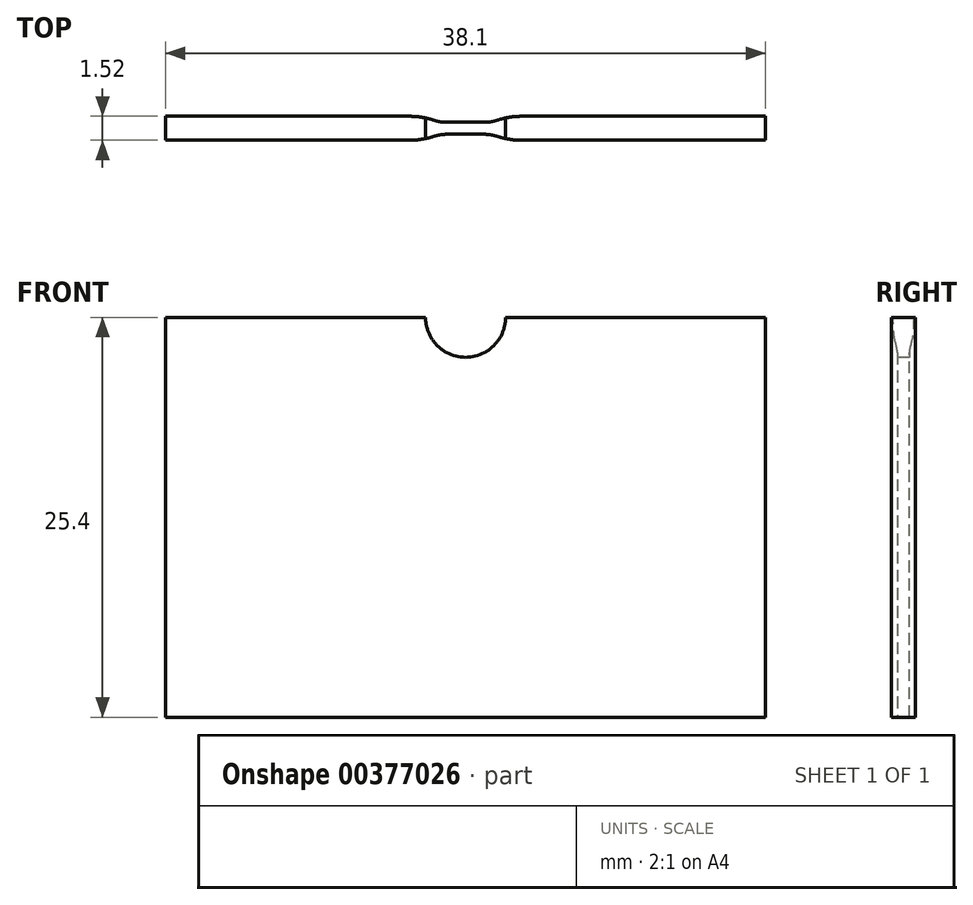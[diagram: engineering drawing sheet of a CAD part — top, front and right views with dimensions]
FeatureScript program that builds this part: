
annotation { "Feature Type Name" : "Feature", "Feature Type Description" : "" }
export const myFeature = defineFeature(function(context is Context, id is Id, definition is map)
    precondition{}
    {
        {
            var Q0;
            Q0=qCreatedBy(makeId("Front.planeOp"),FACE);
            var sketch = newSketch(context, id + "F0", { "sketchPlane" : qUnion([Q0])});
            skLineSegment(sketch, "E0.bottom", {"start": v(0, 0) * mm, "end": v(38.1, 0) * mm});
            skLineSegment(sketch, "E0.top", {"start": v(0, 25.4) * mm, "end": v(38.1, 25.4) * mm});
            skLineSegment(sketch, "E0.left", {"start": v(0, 0) * mm, "end": v(0, 25.4) * mm});
            skLineSegment(sketch, "E0.right", {"start": v(38.1, 0) * mm, "end": v(38.1, 25.4) * mm});
            skSolve(sketch);
        }
        {
            var Q0;
            Q0=makeQuery(id+"F0.imprint","IMPRINT",FACE,{"disambiguationData":[TD([[makeQuery(id+"F0.imprint","IMPRINT",EDGE,{"derivedFrom":sQuery(id+"F0.wireOp",EDGE,"E0.bottom")}),1.0]])]});
            extrude(context, id + "F1", {"entities" : qUnion([Q0]), "depth" : 1.52 * mm});
        }
        {
            var Q0;
            Q0=makeQuery(id+"F1.opExtrude","CAP_FACE",FACE,{"disambiguationData":[OSD([sQuery(id+"F0.wireOp",EDGE,"E0.bottom"),sQuery(id+"F0.wireOp",EDGE,"E0.top"),sQuery(id+"F0.wireOp",EDGE,"E0.left"),sQuery(id+"F0.wireOp",EDGE,"E0.right")])],"isStart":false});
            var sketch = newSketch(context, id + "F2", { "sketchPlane" : qUnion([Q0])});
            skArc(sketch, "E1", {"start": v(16.5, 25.4) * mm, "mid": v(19.05, 22.86) * mm, "end": v(21.59, 25.4) * mm});
            skLineSegment(sketch, "E2", {"start": v(16.5, 25.4) * mm, "end": v(21.59, 25.4) * mm});
            skSolve(sketch);
        }
        {
            var Q0;
            Q0 = qSketchRegion(id + "F2", true);
            extrude(context, id + "F3", {"entities" : qUnion([Q0]), "operationType" : NewBodyOperationType.REMOVE, "oppositeDirection" : true, "depth" : 25.4 * mm});
        }
        {
            var Q0;
            Q0=makeQuery(id+"F1.opExtrude","CAP_EDGE",EDGE,{"disambiguationData":[OSD([sQuery(id+"F0.wireOp",EDGE,"E0.right")])],"isStart":false});
            cPoint(context, id + "F4", {"entities" : qUnion([Q0]), "parameter" : 0.5});
        }
        {
            var Q0;
            Q0=makeQuery(id+"F1.opExtrude","CAP_EDGE",EDGE,{"disambiguationData":[OSD([sQuery(id+"F0.wireOp",EDGE,"E0.left")])],"isStart":false});
            cPoint(context, id + "F5", {"entities" : qUnion([Q0]), "parameter" : 0.5});
        }
        {
            var Q0;
            Q0=makeQuery(id+"F1.opExtrude","CAP_EDGE",EDGE,{"disambiguationData":[OSD([sQuery(id+"F0.wireOp",EDGE,"E0.right")])],"isStart":true});
            cPoint(context, id + "F6", {"entities" : qUnion([Q0]), "parameter" : 0.5});
        }
        {
            var Q0;
            Q0 = qCreatedBy(id + "F4" ,VERTEX);
            var Q1;
            Q1 = qCreatedBy(id + "F5" ,VERTEX);
            var Q2;
            Q2 = qCreatedBy(id + "F6" ,VERTEX);
            cPlane(context, id + "F7", {"entities" : qUnion([Q0, Q1, Q2]), "cplaneType" : CPlaneType.THREE_POINT, "offset" : 25.4 * mm, "width" : 152.4 * mm, "height" : 152.4 * mm});
        }
        {
            var Q0;
            Q0=qCreatedBy(makeId("Top.planeOp"),FACE);
            var sketch = newSketch(context, id + "F8", { "sketchPlane" : qUnion([Q0])});
            skLineSegment(sketch, "E3.0", {"start": v(0, -1.52) * mm, "end": v(16.51, -1.52) * mm});
            skLineSegment(sketch, "E4.0", {"start": v(0, 0) * mm, "end": v(16.51, 0) * mm});
            skLineSegment(sketch, "E5", {"start": v(16.51, -1.52) * mm, "end": v(16.51, -1.14) * mm});
            skLineSegment(sketch, "E6", {"start": v(16.51, -1.14) * mm, "end": v(21.59, -1.14) * mm});
            skLineSegment(sketch, "E7", {"start": v(21.59, -1.14) * mm, "end": v(21.59, -1.52) * mm});
            skLineSegment(sketch, "E8", {"start": v(21.59, 0) * mm, "end": v(21.59, -0.38) * mm});
            skLineSegment(sketch, "E9", {"start": v(21.59, -0.38) * mm, "end": v(16.51, -0.38) * mm});
            skLineSegment(sketch, "E10", {"start": v(16.51, -0.38) * mm, "end": v(16.51, 0) * mm});
            skLineSegment(sketch, "E11", {"start": v(16.51, -1.52) * mm, "end": v(21.59, -1.52) * mm});
            skLineSegment(sketch, "E12", {"start": v(21.59, 0) * mm, "end": v(16.51, 0) * mm});
            skSolve(sketch);
        }
        {
            var Q0;
            Q0 = qSketchRegion(id + "F8", true);
            extrude(context, id + "F9", {"entities" : qUnion([Q0]), "operationType" : NewBodyOperationType.REMOVE, "depth" : 25.4 * mm});
        }
        {
            var Q0;
            Q0=makeQuery(id+"F9.boolean.opBoolean","COPY",EDGE,{"derivedFrom":makeQuery(id+"F9.opExtrude","SWEPT_EDGE",EDGE,{"disambiguationData":[OSD([sQuery(id+"F8.wireOp",EDGE,"E5"),sQuery(id+"F8.wireOp",EDGE,"E6")])]})});
            var Q1;
            Q1=makeQuery(id+"F9.boolean.opBoolean","COPY",EDGE,{"derivedFrom":makeQuery(id+"F9.opExtrude","SWEPT_EDGE",EDGE,{"disambiguationData":[OSD([sQuery(id+"F8.wireOp",EDGE,"E6"),sQuery(id+"F8.wireOp",EDGE,"E7")])]})});
            var Q2;
            Q2=makeQuery(id+"F9.boolean.opBoolean","COPY",EDGE,{"derivedFrom":makeQuery(id+"F9.opExtrude","SWEPT_EDGE",EDGE,{"disambiguationData":[OSD([sQuery(id+"F8.wireOp",EDGE,"E8"),sQuery(id+"F8.wireOp",EDGE,"E9")])]})});
            var Q3;
            Q3=makeQuery(id+"F9.boolean.opBoolean","COPY",EDGE,{"derivedFrom":makeQuery(id+"F9.opExtrude","SWEPT_EDGE",EDGE,{"disambiguationData":[OSD([sQuery(id+"F8.wireOp",EDGE,"E9"),sQuery(id+"F8.wireOp",EDGE,"E10")])]})});
            fillet(context, id + "F10", {"entities" : qUnion([Q0, Q1, Q2, Q3]), "radius" : 2.54 * mm, "tangentPropagation" : true, "allowEdgeOverflow" : false});
        }
        {
            var Q0;
            {var subQ0=sQuery(id+"F0.wireOp",EDGE,"E0.bottom");var subQ1=sQuery(id+"F0.wireOp",EDGE,"E0.top");var subQ2=sQuery(id+"F0.wireOp",EDGE,"E0.left");var subQ3=sQuery(id+"F8.wireOp",EDGE,"E5");Q0=makeQuery(id+"F10.opFillet","BLEND_EDGE",EDGE,{"blendedFrom":[makeQuery(id+"F9.boolean.opBoolean","COPY",EDGE,{"derivedFrom":makeQuery(id+"F9.opExtrude","SWEPT_EDGE",EDGE,{"disambiguationData":[OSD([subQ3,sQuery(id+"F8.wireOp",EDGE,"E6")])]})}),makeQuery(id+"F9.boolean.opBoolean","SPLIT",FACE,{"disambiguationData":[TD([makeQuery(id+"F1.opExtrude","SWEPT_FACE",FACE,{"disambiguationData":[OSD([subQ2])]})])],"derivedFrom":makeQuery(id+"F1.opExtrude","CAP_FACE",FACE,{"disambiguationData":[OSD([subQ0,subQ1,subQ2,sQuery(id+"F0.wireOp",EDGE,"E0.right")])],"isStart":false})})],"blendedInto":[makeQuery(id+"F9.boolean.opBoolean","SPLIT",FACE,{"disambiguationData":[TD([makeQuery(id+"F1.opExtrude","SWEPT_FACE",FACE,{"disambiguationData":[OSD([subQ2])]})])],"derivedFrom":makeQuery(id+"F1.opExtrude","CAP_FACE",FACE,{"disambiguationData":[OSD([subQ0,subQ1,subQ2,sQuery(id+"F0.wireOp",EDGE,"E0.right")])],"isStart":false})})]});}
            var Q1;
            {var subQ0=sQuery(id+"F0.wireOp",EDGE,"E0.bottom");var subQ1=sQuery(id+"F0.wireOp",EDGE,"E0.right");var subQ2=sQuery(id+"F0.wireOp",EDGE,"E0.top");var subQ3=sQuery(id+"F8.wireOp",EDGE,"E7");Q1=makeQuery(id+"F10.opFillet","BLEND_EDGE",EDGE,{"blendedFrom":[makeQuery(id+"F9.boolean.opBoolean","COPY",EDGE,{"derivedFrom":makeQuery(id+"F9.opExtrude","SWEPT_EDGE",EDGE,{"disambiguationData":[OSD([sQuery(id+"F8.wireOp",EDGE,"E6"),subQ3])]})}),makeQuery(id+"F9.boolean.opBoolean","SPLIT",FACE,{"disambiguationData":[TD([makeQuery(id+"F1.opExtrude","SWEPT_FACE",FACE,{"disambiguationData":[OSD([subQ1])]})])],"derivedFrom":makeQuery(id+"F1.opExtrude","CAP_FACE",FACE,{"disambiguationData":[OSD([subQ0,subQ2,sQuery(id+"F0.wireOp",EDGE,"E0.left"),subQ1])],"isStart":false})})],"blendedInto":[makeQuery(id+"F9.boolean.opBoolean","SPLIT",FACE,{"disambiguationData":[TD([makeQuery(id+"F1.opExtrude","SWEPT_FACE",FACE,{"disambiguationData":[OSD([subQ1])]})])],"derivedFrom":makeQuery(id+"F1.opExtrude","CAP_FACE",FACE,{"disambiguationData":[OSD([subQ0,subQ2,sQuery(id+"F0.wireOp",EDGE,"E0.left"),subQ1])],"isStart":false})})]});}
            var Q2;
            {var subQ0=sQuery(id+"F0.wireOp",EDGE,"E0.bottom");var subQ1=sQuery(id+"F0.wireOp",EDGE,"E0.right");var subQ2=sQuery(id+"F0.wireOp",EDGE,"E0.top");var subQ3=sQuery(id+"F8.wireOp",EDGE,"E8");Q2=makeQuery(id+"F10.opFillet","BLEND_EDGE",EDGE,{"blendedFrom":[makeQuery(id+"F9.boolean.opBoolean","COPY",EDGE,{"derivedFrom":makeQuery(id+"F9.opExtrude","SWEPT_EDGE",EDGE,{"disambiguationData":[OSD([subQ3,sQuery(id+"F8.wireOp",EDGE,"E9")])]})}),makeQuery(id+"F9.boolean.opBoolean","SPLIT",FACE,{"disambiguationData":[TD([makeQuery(id+"F1.opExtrude","SWEPT_FACE",FACE,{"disambiguationData":[OSD([subQ1])]})])],"derivedFrom":makeQuery(id+"F1.opExtrude","CAP_FACE",FACE,{"disambiguationData":[OSD([subQ0,subQ2,sQuery(id+"F0.wireOp",EDGE,"E0.left"),subQ1])],"isStart":true})})],"blendedInto":[makeQuery(id+"F9.boolean.opBoolean","SPLIT",FACE,{"disambiguationData":[TD([makeQuery(id+"F1.opExtrude","SWEPT_FACE",FACE,{"disambiguationData":[OSD([subQ1])]})])],"derivedFrom":makeQuery(id+"F1.opExtrude","CAP_FACE",FACE,{"disambiguationData":[OSD([subQ0,subQ2,sQuery(id+"F0.wireOp",EDGE,"E0.left"),subQ1])],"isStart":true})})]});}
            var Q3;
            {var subQ0=sQuery(id+"F0.wireOp",EDGE,"E0.bottom");var subQ1=sQuery(id+"F0.wireOp",EDGE,"E0.top");var subQ2=sQuery(id+"F8.wireOp",EDGE,"E10");var subQ3=sQuery(id+"F0.wireOp",EDGE,"E0.left");Q3=makeQuery(id+"F10.opFillet","BLEND_EDGE",EDGE,{"blendedFrom":[makeQuery(id+"F9.boolean.opBoolean","COPY",EDGE,{"derivedFrom":makeQuery(id+"F9.opExtrude","SWEPT_EDGE",EDGE,{"disambiguationData":[OSD([sQuery(id+"F8.wireOp",EDGE,"E9"),subQ2])]})}),makeQuery(id+"F9.boolean.opBoolean","SPLIT",FACE,{"disambiguationData":[TD([makeQuery(id+"F1.opExtrude","SWEPT_FACE",FACE,{"disambiguationData":[OSD([subQ3])]})])],"derivedFrom":makeQuery(id+"F1.opExtrude","CAP_FACE",FACE,{"disambiguationData":[OSD([subQ0,subQ1,subQ3,sQuery(id+"F0.wireOp",EDGE,"E0.right")])],"isStart":true})})],"blendedInto":[makeQuery(id+"F9.boolean.opBoolean","SPLIT",FACE,{"disambiguationData":[TD([makeQuery(id+"F1.opExtrude","SWEPT_FACE",FACE,{"disambiguationData":[OSD([subQ3])]})])],"derivedFrom":makeQuery(id+"F1.opExtrude","CAP_FACE",FACE,{"disambiguationData":[OSD([subQ0,subQ1,subQ3,sQuery(id+"F0.wireOp",EDGE,"E0.right")])],"isStart":true})})]});}
            fillet(context, id + "F11", {"entities" : qUnion([Q0, Q1, Q2, Q3]), "radius" : 5.08 * mm, "tangentPropagation" : true, "allowEdgeOverflow" : false});
        }
    });
